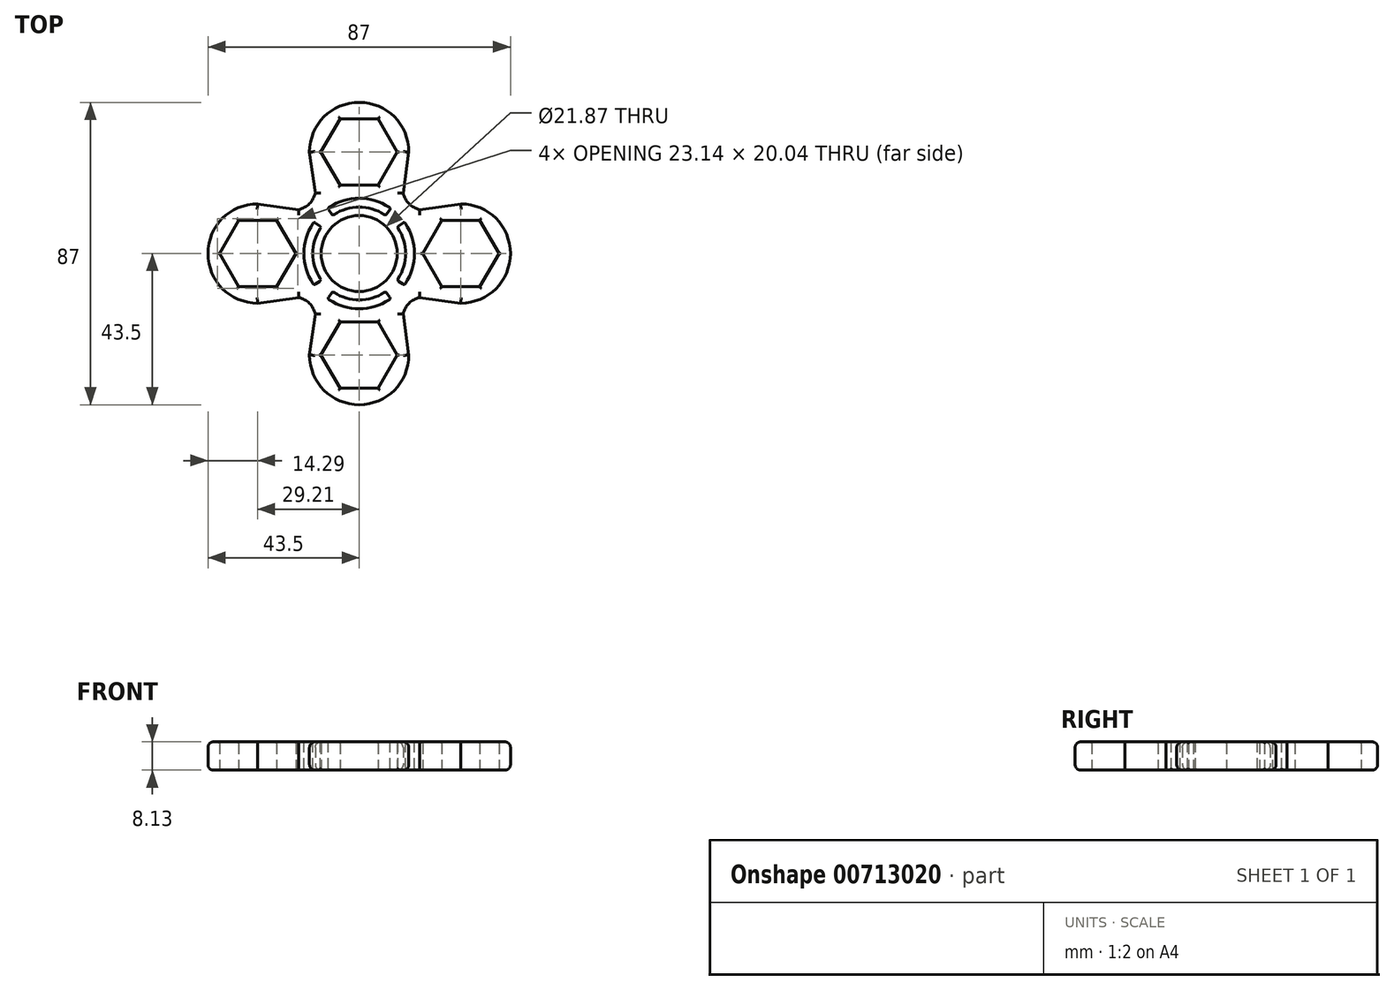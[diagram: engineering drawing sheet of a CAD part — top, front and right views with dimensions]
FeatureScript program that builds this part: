
annotation { "Feature Type Name" : "Feature", "Feature Type Description" : "" }
export const myFeature = defineFeature(function(context is Context, id is Id, definition is map)
    precondition{}
    {
        {
            var Q0;
            Q0=qCreatedBy(makeId("Top.planeOp"),FACE);
            var sketch = newSketch(context, id + "F0", { "sketchPlane" : qUnion([Q0])});
            skCircle(sketch, "E0", {"center": v(0, 0) * mm, "radius": 10.93 * mm});
            skLineSegment(sketch, "E1", {"start": v(0, 32.8) * mm, "end": v(0, -37.97) * mm, "construction": true});
            skLineSegment(sketch, "E2", {"start": v(-47.87, 0) * mm, "end": v(62.97, 0) * mm, "construction": true});
            skCircle(sketch, "E3", {"center": v(29.21, 0) * mm, "radius": 7.94 * mm});
            skCircle(sketch, "E4", {"center": v(0, 29.21) * mm, "radius": 7.94 * mm});
            skCircle(sketch, "E5", {"center": v(-29.21, 0) * mm, "radius": 7.94 * mm});
            skCircle(sketch, "E6", {"center": v(0, -29.21) * mm, "radius": 7.94 * mm});
            skArc(sketch, "E7", {"start": v(14.29, 29.21) * mm, "mid": v(0, 43.5) * mm, "end": v(-14.29, 29.21) * mm});
            skArc(sketch, "E8", {"start": v(29.21, -14.29) * mm, "mid": v(43.5, 0) * mm, "end": v(29.21, 14.29) * mm});
            skArc(sketch, "E9", {"start": v(-14.29, -29.21) * mm, "mid": v(0, -43.5) * mm, "end": v(14.29, -29.21) * mm});
            skArc(sketch, "E10", {"start": v(-29.21, 14.29) * mm, "mid": v(-43.5, 0) * mm, "end": v(-29.21, -14.29) * mm});
            skPoint(sketch, "E11.visualSharp", {"position": v(-11.05, 11.05) * mm});
            skArc(sketch, "E11.filletArc", {"start": v(-17.4, 12.64) * mm, "mid": v(-14.33, 14.33) * mm, "end": v(-12.64, 17.4) * mm});
            skPoint(sketch, "E12.visualSharp", {"position": v(11.05, 11.05) * mm});
            skArc(sketch, "E12.filletArc", {"start": v(12.64, 17.4) * mm, "mid": v(14.33, 14.33) * mm, "end": v(17.4, 12.64) * mm});
            skArc(sketch, "E13.MirrorCS", {"start": v(-17.4, -12.64) * mm, "mid": v(-14.33, -14.33) * mm, "end": v(-12.64, -17.4) * mm});
            skArc(sketch, "E14.MirrorCS", {"start": v(12.64, -17.4) * mm, "mid": v(14.33, -14.33) * mm, "end": v(17.4, -12.64) * mm});
            skLineSegment(sketch, "E15", {"start": v(-14.29, -29.21) * mm, "end": v(-12.64, -17.4) * mm});
            skLineSegment(sketch, "E16", {"start": v(14.29, -29.2) * mm, "end": v(12.64, -17.4) * mm});
            skLineSegment(sketch, "E17", {"start": v(17.4, -12.64) * mm, "end": v(29.21, -14.29) * mm});
            skLineSegment(sketch, "E18", {"start": v(17.4, 12.64) * mm, "end": v(29.21, 14.29) * mm});
            skLineSegment(sketch, "E19", {"start": v(12.64, 17.4) * mm, "end": v(14.29, 29.21) * mm});
            skLineSegment(sketch, "E20", {"start": v(-14.29, 29.21) * mm, "end": v(-12.64, 17.4) * mm});
            skLineSegment(sketch, "E21", {"start": v(-17.4, 12.64) * mm, "end": v(-29.2, 14.29) * mm});
            skLineSegment(sketch, "E22", {"start": v(-29.2, -14.29) * mm, "end": v(-17.4, -12.64) * mm});
            skCircle(sketch, "E23.cCircle", {"center": v(0, 29.21) * mm, "radius": 9.51 * mm, "construction": true});
            skLineSegment(sketch, "E23.0", {"start": v(10.99, 29.21) * mm, "end": v(5.5, 19.7) * mm});
            skLineSegment(sketch, "E23.1", {"start": v(5.5, 19.7) * mm, "end": v(-5.5, 19.7) * mm});
            skLineSegment(sketch, "E23.2", {"start": v(-5.5, 19.7) * mm, "end": v(-10.99, 29.21) * mm});
            skLineSegment(sketch, "E23.3", {"start": v(-10.99, 29.21) * mm, "end": v(-5.5, 38.72) * mm});
            skLineSegment(sketch, "E23.4", {"start": v(-5.5, 38.72) * mm, "end": v(5.5, 38.72) * mm});
            skLineSegment(sketch, "E23.5", {"start": v(5.5, 38.72) * mm, "end": v(10.99, 29.21) * mm});
            skPoint(sketch, "E23.0.midPoint", {"position": v(8.24, 24.45) * mm});
            skCircle(sketch, "E24.cCircle", {"center": v(29.21, 0) * mm, "radius": 9.51 * mm, "construction": true});
            skLineSegment(sketch, "E24.0", {"start": v(40.2, 0) * mm, "end": v(34.7, -9.51) * mm});
            skLineSegment(sketch, "E24.1", {"start": v(34.7, -9.51) * mm, "end": v(23.72, -9.51) * mm});
            skLineSegment(sketch, "E24.2", {"start": v(23.72, -9.51) * mm, "end": v(18.22, 0) * mm});
            skLineSegment(sketch, "E24.3", {"start": v(18.22, 0) * mm, "end": v(23.72, 9.51) * mm});
            skLineSegment(sketch, "E24.4", {"start": v(23.72, 9.51) * mm, "end": v(34.7, 9.51) * mm});
            skLineSegment(sketch, "E24.5", {"start": v(34.7, 9.51) * mm, "end": v(40.2, 0) * mm});
            skPoint(sketch, "E24.0.midPoint", {"position": v(37.45, -4.76) * mm});
            skCircle(sketch, "E25.cCircle", {"center": v(0, -29.21) * mm, "radius": 9.51 * mm, "construction": true});
            skLineSegment(sketch, "E25.0", {"start": v(10.99, -29.2) * mm, "end": v(5.5, -38.72) * mm});
            skLineSegment(sketch, "E25.1", {"start": v(5.5, -38.72) * mm, "end": v(-5.5, -38.72) * mm});
            skLineSegment(sketch, "E25.2", {"start": v(-5.5, -38.72) * mm, "end": v(-10.99, -29.2) * mm});
            skLineSegment(sketch, "E25.3", {"start": v(-10.99, -29.21) * mm, "end": v(-5.5, -19.7) * mm});
            skLineSegment(sketch, "E25.4", {"start": v(-5.5, -19.7) * mm, "end": v(5.5, -19.7) * mm});
            skLineSegment(sketch, "E25.5", {"start": v(5.5, -19.7) * mm, "end": v(10.99, -29.21) * mm});
            skPoint(sketch, "E25.0.midPoint", {"position": v(8.24, -33.97) * mm});
            skPoint(sketch, "E26.0.midPoint", {"position": v(-0.58, -16.53) * mm});
            skCircle(sketch, "E27.cCircle", {"center": v(-29.21, 0) * mm, "radius": 9.51 * mm, "construction": true});
            skLineSegment(sketch, "E27.0", {"start": v(-18.22, 0) * mm, "end": v(-23.72, -9.51) * mm});
            skLineSegment(sketch, "E27.1", {"start": v(-23.72, -9.51) * mm, "end": v(-34.7, -9.51) * mm});
            skLineSegment(sketch, "E27.2", {"start": v(-34.7, -9.51) * mm, "end": v(-40.2, 0) * mm});
            skLineSegment(sketch, "E27.3", {"start": v(-40.2, 0) * mm, "end": v(-34.7, 9.51) * mm});
            skLineSegment(sketch, "E27.4", {"start": v(-34.7, 9.51) * mm, "end": v(-23.72, 9.51) * mm});
            skLineSegment(sketch, "E27.5", {"start": v(-23.72, 9.51) * mm, "end": v(-18.22, 0) * mm});
            skPoint(sketch, "E27.0.midPoint", {"position": v(-20.97, -4.76) * mm});
            skSolve(sketch);
        }
        {
            var Q0;
            Q0=qSketchRegion(id+"F0",true);
            extrude(context, id + "F1", {"entities" : qUnion([Q0]), "depth" : 8.13 * mm, "offsetDistance" : 25.4 * mm});
        }
        {
            var Q0;
            Q0=makeQuery(id+"F1.opExtrude","CAP_EDGE",EDGE,{"disambiguationData":[OSD([sQuery(id+"F0.wireOp",EDGE,"E10")])],"isStart":true});
            var Q1;
            Q1=makeQuery(id+"F1.opExtrude","CAP_EDGE",EDGE,{"disambiguationData":[OSD([sQuery(id+"F0.wireOp",EDGE,"E22")])],"isStart":true});
            var Q2;
            Q2=makeQuery(id+"F1.opExtrude","CAP_EDGE",EDGE,{"disambiguationData":[OSD([sQuery(id+"F0.wireOp",EDGE,"E13.MirrorCS")])],"isStart":true});
            var Q3;
            Q3=makeQuery(id+"F1.opExtrude","CAP_EDGE",EDGE,{"disambiguationData":[OSD([sQuery(id+"F0.wireOp",EDGE,"E15")])],"isStart":true});
            var Q4;
            Q4=makeQuery(id+"F1.opExtrude","CAP_EDGE",EDGE,{"disambiguationData":[OSD([sQuery(id+"F0.wireOp",EDGE,"E9")])],"isStart":true});
            var Q5;
            Q5=makeQuery(id+"F1.opExtrude","CAP_EDGE",EDGE,{"disambiguationData":[OSD([sQuery(id+"F0.wireOp",EDGE,"E16")])],"isStart":true});
            var Q6;
            Q6=makeQuery(id+"F1.opExtrude","CAP_EDGE",EDGE,{"disambiguationData":[OSD([sQuery(id+"F0.wireOp",EDGE,"E14.MirrorCS")])],"isStart":true});
            var Q7;
            Q7=makeQuery(id+"F1.opExtrude","CAP_EDGE",EDGE,{"disambiguationData":[OSD([sQuery(id+"F0.wireOp",EDGE,"E17")])],"isStart":true});
            var Q8;
            Q8=makeQuery(id+"F1.opExtrude","CAP_EDGE",EDGE,{"disambiguationData":[OSD([sQuery(id+"F0.wireOp",EDGE,"E8")])],"isStart":true});
            var Q9;
            Q9=makeQuery(id+"F1.opExtrude","CAP_EDGE",EDGE,{"disambiguationData":[OSD([sQuery(id+"F0.wireOp",EDGE,"E18")])],"isStart":true});
            var Q10;
            Q10=makeQuery(id+"F1.opExtrude","CAP_EDGE",EDGE,{"disambiguationData":[OSD([sQuery(id+"F0.wireOp",EDGE,"E12.filletArc")])],"isStart":true});
            var Q11;
            Q11=makeQuery(id+"F1.opExtrude","CAP_EDGE",EDGE,{"disambiguationData":[OSD([sQuery(id+"F0.wireOp",EDGE,"E19")])],"isStart":true});
            var Q12;
            Q12=makeQuery(id+"F1.opExtrude","CAP_EDGE",EDGE,{"disambiguationData":[OSD([sQuery(id+"F0.wireOp",EDGE,"E7")])],"isStart":true});
            var Q13;
            Q13=makeQuery(id+"F1.opExtrude","CAP_EDGE",EDGE,{"disambiguationData":[OSD([sQuery(id+"F0.wireOp",EDGE,"E20")])],"isStart":true});
            var Q14;
            Q14=makeQuery(id+"F1.opExtrude","CAP_EDGE",EDGE,{"disambiguationData":[OSD([sQuery(id+"F0.wireOp",EDGE,"E11.filletArc")])],"isStart":true});
            var Q15;
            Q15=makeQuery(id+"F1.opExtrude","CAP_EDGE",EDGE,{"disambiguationData":[OSD([sQuery(id+"F0.wireOp",EDGE,"E21")])],"isStart":true});
            var Q16;
            Q16=makeQuery(id+"F1.opExtrude","CAP_EDGE",EDGE,{"disambiguationData":[OSD([sQuery(id+"F0.wireOp",EDGE,"E10")])],"isStart":false});
            var Q17;
            Q17=makeQuery(id+"F1.opExtrude","CAP_EDGE",EDGE,{"disambiguationData":[OSD([sQuery(id+"F0.wireOp",EDGE,"E22")])],"isStart":false});
            var Q18;
            Q18=makeQuery(id+"F1.opExtrude","CAP_EDGE",EDGE,{"disambiguationData":[OSD([sQuery(id+"F0.wireOp",EDGE,"E13.MirrorCS")])],"isStart":false});
            var Q19;
            Q19=makeQuery(id+"F1.opExtrude","CAP_EDGE",EDGE,{"disambiguationData":[OSD([sQuery(id+"F0.wireOp",EDGE,"E21")])],"isStart":false});
            var Q20;
            Q20=makeQuery(id+"F1.opExtrude","CAP_EDGE",EDGE,{"disambiguationData":[OSD([sQuery(id+"F0.wireOp",EDGE,"E11.filletArc")])],"isStart":false});
            var Q21;
            Q21=makeQuery(id+"F1.opExtrude","CAP_EDGE",EDGE,{"disambiguationData":[OSD([sQuery(id+"F0.wireOp",EDGE,"E20")])],"isStart":false});
            var Q22;
            Q22=makeQuery(id+"F1.opExtrude","CAP_EDGE",EDGE,{"disambiguationData":[OSD([sQuery(id+"F0.wireOp",EDGE,"E7")])],"isStart":false});
            var Q23;
            Q23=makeQuery(id+"F1.opExtrude","CAP_EDGE",EDGE,{"disambiguationData":[OSD([sQuery(id+"F0.wireOp",EDGE,"E19")])],"isStart":false});
            var Q24;
            Q24=makeQuery(id+"F1.opExtrude","CAP_EDGE",EDGE,{"disambiguationData":[OSD([sQuery(id+"F0.wireOp",EDGE,"E8")])],"isStart":false});
            var Q25;
            Q25=makeQuery(id+"F1.opExtrude","CAP_EDGE",EDGE,{"disambiguationData":[OSD([sQuery(id+"F0.wireOp",EDGE,"E17")])],"isStart":false});
            var Q26;
            Q26=makeQuery(id+"F1.opExtrude","CAP_EDGE",EDGE,{"disambiguationData":[OSD([sQuery(id+"F0.wireOp",EDGE,"E14.MirrorCS")])],"isStart":false});
            var Q27;
            Q27=makeQuery(id+"F1.opExtrude","CAP_EDGE",EDGE,{"disambiguationData":[OSD([sQuery(id+"F0.wireOp",EDGE,"E16")])],"isStart":false});
            var Q28;
            Q28=makeQuery(id+"F1.opExtrude","CAP_EDGE",EDGE,{"disambiguationData":[OSD([sQuery(id+"F0.wireOp",EDGE,"E9")])],"isStart":false});
            var Q29;
            Q29=makeQuery(id+"F1.opExtrude","CAP_EDGE",EDGE,{"disambiguationData":[OSD([sQuery(id+"F0.wireOp",EDGE,"E15")])],"isStart":false});
            var Q30;
            Q30=makeQuery(id+"F1.opExtrude","CAP_EDGE",EDGE,{"disambiguationData":[OSD([sQuery(id+"F0.wireOp",EDGE,"E12.filletArc")])],"isStart":false});
            var Q31;
            Q31=makeQuery(id+"F1.opExtrude","CAP_EDGE",EDGE,{"disambiguationData":[OSD([sQuery(id+"F0.wireOp",EDGE,"E18")])],"isStart":false});
            fillet(context, id + "F2", {"entities" : qUnion([Q0, Q1, Q2, Q3, Q4, Q5, Q6, Q7, Q8, Q9, Q10, Q11, Q12, Q13, Q14, Q15, Q16, Q17, Q18, Q19, Q20, Q21, Q22, Q23, Q24, Q25, Q26, Q27, Q28, Q29, Q30, Q31]), "radius" : 1.57 * mm, "allowEdgeOverflow" : false});
        }
        {
            var Q0;
            Q0=makeQuery(id+"F1.opExtrude","CAP_EDGE",EDGE,{"disambiguationData":[OSD([sQuery(id+"F0.wireOp",EDGE,"E5")])],"isStart":false});
            var Q1;
            Q1=makeQuery(id+"F1.opExtrude","CAP_EDGE",EDGE,{"disambiguationData":[OSD([sQuery(id+"F0.wireOp",EDGE,"E4")])],"isStart":false});
            var Q2;
            Q2=makeQuery(id+"F1.opExtrude","CAP_EDGE",EDGE,{"disambiguationData":[OSD([sQuery(id+"F0.wireOp",EDGE,"E0")])],"isStart":false});
            var Q3;
            Q3=makeQuery(id+"F1.opExtrude","CAP_EDGE",EDGE,{"disambiguationData":[OSD([sQuery(id+"F0.wireOp",EDGE,"E3")])],"isStart":false});
            var Q4;
            Q4=makeQuery(id+"F1.opExtrude","CAP_EDGE",EDGE,{"disambiguationData":[OSD([sQuery(id+"F0.wireOp",EDGE,"E6")])],"isStart":false});
            var Q5;
            Q5=makeQuery(id+"F1.opExtrude","CAP_EDGE",EDGE,{"disambiguationData":[OSD([sQuery(id+"F0.wireOp",EDGE,"E6")])],"isStart":true});
            var Q6;
            Q6=makeQuery(id+"F1.opExtrude","CAP_EDGE",EDGE,{"disambiguationData":[OSD([sQuery(id+"F0.wireOp",EDGE,"E5")])],"isStart":true});
            var Q7;
            Q7=makeQuery(id+"F1.opExtrude","CAP_EDGE",EDGE,{"disambiguationData":[OSD([sQuery(id+"F0.wireOp",EDGE,"E0")])],"isStart":true});
            var Q8;
            Q8=makeQuery(id+"F1.opExtrude","CAP_EDGE",EDGE,{"disambiguationData":[OSD([sQuery(id+"F0.wireOp",EDGE,"E3")])],"isStart":true});
            var Q9;
            Q9=makeQuery(id+"F1.opExtrude","CAP_EDGE",EDGE,{"disambiguationData":[OSD([sQuery(id+"F0.wireOp",EDGE,"E4")])],"isStart":true});
            fillet(context, id + "F3", {"entities" : qUnion([Q0, Q1, Q2, Q3, Q4, Q5, Q6, Q7, Q8, Q9]), "radius" : 0.5 * mm, "tangentPropagation" : true, "allowEdgeOverflow" : false});
        }
        {
            var Q0;
            Q0=makeQuery(id+"F1.opExtrude","CAP_EDGE",EDGE,{"disambiguationData":[OSD([sQuery(id+"F0.wireOp",EDGE,"E25.4")])],"isStart":false});
            var Q1;
            Q1=makeQuery(id+"F1.opExtrude","CAP_EDGE",EDGE,{"disambiguationData":[OSD([sQuery(id+"F0.wireOp",EDGE,"E24.4")])],"isStart":false});
            var Q2;
            Q2=makeQuery(id+"F1.opExtrude","CAP_EDGE",EDGE,{"disambiguationData":[OSD([sQuery(id+"F0.wireOp",EDGE,"E23.5")])],"isStart":false});
            var Q3;
            Q3=makeQuery(id+"F1.opExtrude","CAP_EDGE",EDGE,{"disambiguationData":[OSD([sQuery(id+"F0.wireOp",EDGE,"E27.5")])],"isStart":false});
            var Q4;
            Q4=makeQuery(id+"F1.opExtrude","CAP_EDGE",EDGE,{"disambiguationData":[OSD([sQuery(id+"F0.wireOp",EDGE,"E27.4")])],"isStart":false});
            var Q5;
            Q5=makeQuery(id+"F1.opExtrude","CAP_EDGE",EDGE,{"disambiguationData":[OSD([sQuery(id+"F0.wireOp",EDGE,"E27.3")])],"isStart":false});
            var Q6;
            Q6=makeQuery(id+"F1.opExtrude","CAP_EDGE",EDGE,{"disambiguationData":[OSD([sQuery(id+"F0.wireOp",EDGE,"E27.2")])],"isStart":false});
            var Q7;
            Q7=makeQuery(id+"F1.opExtrude","CAP_EDGE",EDGE,{"disambiguationData":[OSD([sQuery(id+"F0.wireOp",EDGE,"E27.1")])],"isStart":false});
            var Q8;
            Q8=makeQuery(id+"F1.opExtrude","CAP_EDGE",EDGE,{"disambiguationData":[OSD([sQuery(id+"F0.wireOp",EDGE,"E27.0")])],"isStart":false});
            var Q9;
            Q9=makeQuery(id+"F1.opExtrude","CAP_EDGE",EDGE,{"disambiguationData":[OSD([sQuery(id+"F0.wireOp",EDGE,"E25.3")])],"isStart":false});
            var Q10;
            Q10=makeQuery(id+"F1.opExtrude","CAP_EDGE",EDGE,{"disambiguationData":[OSD([sQuery(id+"F0.wireOp",EDGE,"E25.5")])],"isStart":false});
            var Q11;
            Q11=makeQuery(id+"F1.opExtrude","CAP_EDGE",EDGE,{"disambiguationData":[OSD([sQuery(id+"F0.wireOp",EDGE,"E25.0")])],"isStart":false});
            var Q12;
            Q12=makeQuery(id+"F1.opExtrude","CAP_EDGE",EDGE,{"disambiguationData":[OSD([sQuery(id+"F0.wireOp",EDGE,"E25.1")])],"isStart":false});
            var Q13;
            Q13=makeQuery(id+"F1.opExtrude","CAP_EDGE",EDGE,{"disambiguationData":[OSD([sQuery(id+"F0.wireOp",EDGE,"E25.2")])],"isStart":false});
            var Q14;
            Q14=makeQuery(id+"F1.opExtrude","CAP_EDGE",EDGE,{"disambiguationData":[OSD([sQuery(id+"F0.wireOp",EDGE,"E24.3")])],"isStart":false});
            var Q15;
            Q15=makeQuery(id+"F1.opExtrude","CAP_EDGE",EDGE,{"disambiguationData":[OSD([sQuery(id+"F0.wireOp",EDGE,"E24.2")])],"isStart":false});
            var Q16;
            Q16=makeQuery(id+"F1.opExtrude","CAP_EDGE",EDGE,{"disambiguationData":[OSD([sQuery(id+"F0.wireOp",EDGE,"E24.1")])],"isStart":false});
            var Q17;
            Q17=makeQuery(id+"F1.opExtrude","CAP_EDGE",EDGE,{"disambiguationData":[OSD([sQuery(id+"F0.wireOp",EDGE,"E24.0")])],"isStart":false});
            var Q18;
            Q18=makeQuery(id+"F1.opExtrude","CAP_EDGE",EDGE,{"disambiguationData":[OSD([sQuery(id+"F0.wireOp",EDGE,"E24.5")])],"isStart":false});
            var Q19;
            Q19=makeQuery(id+"F1.opExtrude","CAP_EDGE",EDGE,{"disambiguationData":[OSD([sQuery(id+"F0.wireOp",EDGE,"E23.0")])],"isStart":false});
            var Q20;
            Q20=makeQuery(id+"F1.opExtrude","CAP_EDGE",EDGE,{"disambiguationData":[OSD([sQuery(id+"F0.wireOp",EDGE,"E23.1")])],"isStart":false});
            var Q21;
            Q21=makeQuery(id+"F1.opExtrude","CAP_EDGE",EDGE,{"disambiguationData":[OSD([sQuery(id+"F0.wireOp",EDGE,"E23.2")])],"isStart":false});
            var Q22;
            Q22=makeQuery(id+"F1.opExtrude","CAP_EDGE",EDGE,{"disambiguationData":[OSD([sQuery(id+"F0.wireOp",EDGE,"E23.3")])],"isStart":false});
            var Q23;
            Q23=makeQuery(id+"F1.opExtrude","CAP_EDGE",EDGE,{"disambiguationData":[OSD([sQuery(id+"F0.wireOp",EDGE,"E23.4")])],"isStart":false});
            var Q24;
            Q24=makeQuery(id+"F1.opExtrude","CAP_EDGE",EDGE,{"disambiguationData":[OSD([sQuery(id+"F0.wireOp",EDGE,"E27.2")])],"isStart":true});
            var Q25;
            Q25=makeQuery(id+"F1.opExtrude","CAP_EDGE",EDGE,{"disambiguationData":[OSD([sQuery(id+"F0.wireOp",EDGE,"E27.1")])],"isStart":true});
            var Q26;
            Q26=makeQuery(id+"F1.opExtrude","CAP_EDGE",EDGE,{"disambiguationData":[OSD([sQuery(id+"F0.wireOp",EDGE,"E27.0")])],"isStart":true});
            var Q27;
            Q27=makeQuery(id+"F1.opExtrude","CAP_EDGE",EDGE,{"disambiguationData":[OSD([sQuery(id+"F0.wireOp",EDGE,"E27.5")])],"isStart":true});
            var Q28;
            Q28=makeQuery(id+"F1.opExtrude","CAP_EDGE",EDGE,{"disambiguationData":[OSD([sQuery(id+"F0.wireOp",EDGE,"E27.4")])],"isStart":true});
            var Q29;
            Q29=makeQuery(id+"F1.opExtrude","CAP_EDGE",EDGE,{"disambiguationData":[OSD([sQuery(id+"F0.wireOp",EDGE,"E27.3")])],"isStart":true});
            var Q30;
            Q30=makeQuery(id+"F1.opExtrude","CAP_EDGE",EDGE,{"disambiguationData":[OSD([sQuery(id+"F0.wireOp",EDGE,"E23.2")])],"isStart":true});
            var Q31;
            Q31=makeQuery(id+"F1.opExtrude","CAP_EDGE",EDGE,{"disambiguationData":[OSD([sQuery(id+"F0.wireOp",EDGE,"E23.1")])],"isStart":true});
            var Q32;
            Q32=makeQuery(id+"F1.opExtrude","CAP_EDGE",EDGE,{"disambiguationData":[OSD([sQuery(id+"F0.wireOp",EDGE,"E23.0")])],"isStart":true});
            var Q33;
            Q33=makeQuery(id+"F1.opExtrude","CAP_EDGE",EDGE,{"disambiguationData":[OSD([sQuery(id+"F0.wireOp",EDGE,"E23.5")])],"isStart":true});
            var Q34;
            Q34=makeQuery(id+"F1.opExtrude","CAP_EDGE",EDGE,{"disambiguationData":[OSD([sQuery(id+"F0.wireOp",EDGE,"E23.4")])],"isStart":true});
            var Q35;
            Q35=makeQuery(id+"F1.opExtrude","CAP_EDGE",EDGE,{"disambiguationData":[OSD([sQuery(id+"F0.wireOp",EDGE,"E23.3")])],"isStart":true});
            var Q36;
            Q36=makeQuery(id+"F1.opExtrude","CAP_EDGE",EDGE,{"disambiguationData":[OSD([sQuery(id+"F0.wireOp",EDGE,"E24.2")])],"isStart":true});
            var Q37;
            Q37=makeQuery(id+"F1.opExtrude","CAP_EDGE",EDGE,{"disambiguationData":[OSD([sQuery(id+"F0.wireOp",EDGE,"E24.1")])],"isStart":true});
            var Q38;
            Q38=makeQuery(id+"F1.opExtrude","CAP_EDGE",EDGE,{"disambiguationData":[OSD([sQuery(id+"F0.wireOp",EDGE,"E24.0")])],"isStart":true});
            var Q39;
            Q39=makeQuery(id+"F1.opExtrude","CAP_EDGE",EDGE,{"disambiguationData":[OSD([sQuery(id+"F0.wireOp",EDGE,"E24.5")])],"isStart":true});
            var Q40;
            Q40=makeQuery(id+"F1.opExtrude","CAP_EDGE",EDGE,{"disambiguationData":[OSD([sQuery(id+"F0.wireOp",EDGE,"E24.4")])],"isStart":true});
            var Q41;
            Q41=makeQuery(id+"F1.opExtrude","CAP_EDGE",EDGE,{"disambiguationData":[OSD([sQuery(id+"F0.wireOp",EDGE,"E24.3")])],"isStart":true});
            var Q42;
            Q42=makeQuery(id+"F1.opExtrude","CAP_EDGE",EDGE,{"disambiguationData":[OSD([sQuery(id+"F0.wireOp",EDGE,"E25.4")])],"isStart":true});
            var Q43;
            Q43=makeQuery(id+"F1.opExtrude","CAP_EDGE",EDGE,{"disambiguationData":[OSD([sQuery(id+"F0.wireOp",EDGE,"E25.3")])],"isStart":true});
            var Q44;
            Q44=makeQuery(id+"F1.opExtrude","CAP_EDGE",EDGE,{"disambiguationData":[OSD([sQuery(id+"F0.wireOp",EDGE,"E25.2")])],"isStart":true});
            var Q45;
            Q45=makeQuery(id+"F1.opExtrude","CAP_EDGE",EDGE,{"disambiguationData":[OSD([sQuery(id+"F0.wireOp",EDGE,"E25.1")])],"isStart":true});
            var Q46;
            Q46=makeQuery(id+"F1.opExtrude","CAP_EDGE",EDGE,{"disambiguationData":[OSD([sQuery(id+"F0.wireOp",EDGE,"E25.0")])],"isStart":true});
            var Q47;
            Q47=makeQuery(id+"F1.opExtrude","CAP_EDGE",EDGE,{"disambiguationData":[OSD([sQuery(id+"F0.wireOp",EDGE,"E25.5")])],"isStart":true});
            fillet(context, id + "F4", {"entities" : qUnion([Q0, Q1, Q2, Q3, Q4, Q5, Q6, Q7, Q8, Q9, Q10, Q11, Q12, Q13, Q14, Q15, Q16, Q17, Q18, Q19, Q20, Q21, Q22, Q23, Q24, Q25, Q26, Q27, Q28, Q29, Q30, Q31, Q32, Q33, Q34, Q35, Q36, Q37, Q38, Q39, Q40, Q41, Q42, Q43, Q44, Q45, Q46, Q47]), "radius" : 0.5 * mm, "tangentPropagation" : true, "allowEdgeOverflow" : false});
        }
        {
            var Q0;
            Q0=makeQuery(id+"F1.opExtrude","CAP_FACE",FACE,{"disambiguationData":[OSD([sQuery(id+"F0.wireOp",EDGE,"E0"),sQuery(id+"F0.wireOp",EDGE,"E7"),sQuery(id+"F0.wireOp",EDGE,"E8"),sQuery(id+"F0.wireOp",EDGE,"E9"),sQuery(id+"F0.wireOp",EDGE,"E10"),sQuery(id+"F0.wireOp",EDGE,"E11.filletArc"),sQuery(id+"F0.wireOp",EDGE,"E12.filletArc"),sQuery(id+"F0.wireOp",EDGE,"E13.MirrorCS"),sQuery(id+"F0.wireOp",EDGE,"E14.MirrorCS"),sQuery(id+"F0.wireOp",EDGE,"E15"),sQuery(id+"F0.wireOp",EDGE,"E16"),sQuery(id+"F0.wireOp",EDGE,"E17"),sQuery(id+"F0.wireOp",EDGE,"E18"),sQuery(id+"F0.wireOp",EDGE,"E19"),sQuery(id+"F0.wireOp",EDGE,"E20"),sQuery(id+"F0.wireOp",EDGE,"E21"),sQuery(id+"F0.wireOp",EDGE,"E22"),sQuery(id+"F0.wireOp",EDGE,"E23.0"),sQuery(id+"F0.wireOp",EDGE,"E23.1"),sQuery(id+"F0.wireOp",EDGE,"E23.2"),sQuery(id+"F0.wireOp",EDGE,"E23.3"),sQuery(id+"F0.wireOp",EDGE,"E23.4"),sQuery(id+"F0.wireOp",EDGE,"E23.5"),sQuery(id+"F0.wireOp",EDGE,"E24.0"),sQuery(id+"F0.wireOp",EDGE,"E24.1"),sQuery(id+"F0.wireOp",EDGE,"E24.2"),sQuery(id+"F0.wireOp",EDGE,"E24.3"),sQuery(id+"F0.wireOp",EDGE,"E24.4"),sQuery(id+"F0.wireOp",EDGE,"E24.5"),sQuery(id+"F0.wireOp",EDGE,"E25.0"),sQuery(id+"F0.wireOp",EDGE,"E25.1"),sQuery(id+"F0.wireOp",EDGE,"E25.2"),sQuery(id+"F0.wireOp",EDGE,"E25.3"),sQuery(id+"F0.wireOp",EDGE,"E25.4"),sQuery(id+"F0.wireOp",EDGE,"E25.5"),sQuery(id+"F0.wireOp",EDGE,"E27.0"),sQuery(id+"F0.wireOp",EDGE,"E27.1"),sQuery(id+"F0.wireOp",EDGE,"E27.2"),sQuery(id+"F0.wireOp",EDGE,"E27.3"),sQuery(id+"F0.wireOp",EDGE,"E27.4"),sQuery(id+"F0.wireOp",EDGE,"E27.5")])],"isStart":false});
            var sketch = newSketch(context, id + "F5", { "sketchPlane" : qUnion([Q0])});
            skLineSegment(sketch, "E28", {"start": v(0, 19.96) * mm, "end": v(0, -20.08) * mm, "construction": true});
            skLineSegment(sketch, "E29", {"start": v(-9.1, 13) * mm, "end": v(-7.65, 10.92) * mm});
            skLineSegment(sketch, "E30", {"start": v(9.1, 13) * mm, "end": v(7.65, 10.92) * mm});
            skArc(sketch, "E31", {"start": v(9.1, 13) * mm, "mid": v(0, 15.88) * mm, "end": v(-9.1, 13) * mm});
            skArc(sketch, "E32", {"start": v(7.65, 10.92) * mm, "mid": v(0, 13.34) * mm, "end": v(-7.65, 10.92) * mm});
            skArc(sketch, "E33.1.0", {"start": v(-13, 9.1) * mm, "mid": v(-15.88, 0) * mm, "end": v(-13, -9.1) * mm});
            skLineSegment(sketch, "E33.1.1", {"start": v(-13, -9.1) * mm, "end": v(-10.92, -7.65) * mm});
            skArc(sketch, "E33.1.2", {"start": v(-10.92, 7.65) * mm, "mid": v(-13.34, 0) * mm, "end": v(-10.92, -7.65) * mm});
            skLineSegment(sketch, "E33.1.3", {"start": v(-13, 9.1) * mm, "end": v(-10.92, 7.65) * mm});
            skArc(sketch, "E33.2.0", {"start": v(-9.1, -13) * mm, "mid": v(0, -15.87) * mm, "end": v(9.1, -13) * mm});
            skLineSegment(sketch, "E33.2.1", {"start": v(9.1, -13) * mm, "end": v(7.65, -10.92) * mm});
            skArc(sketch, "E33.2.2", {"start": v(-7.65, -10.92) * mm, "mid": v(0, -13.33) * mm, "end": v(7.65, -10.92) * mm});
            skLineSegment(sketch, "E33.2.3", {"start": v(-9.1, -13) * mm, "end": v(-7.65, -10.92) * mm});
            skLineSegment(sketch, "E34.4.3.0", {"start": v(13, 9.1) * mm, "end": v(10.92, 7.65) * mm});
            skArc(sketch, "E34.6.3.0", {"start": v(13, -9.1) * mm, "mid": v(15.87, 0) * mm, "end": v(13, 9.1) * mm});
            skArc(sketch, "E34.7.3.0", {"start": v(10.92, -7.65) * mm, "mid": v(13.34, 0) * mm, "end": v(10.92, 7.65) * mm});
            skLineSegment(sketch, "E34.11.3.0", {"start": v(13, -9.1) * mm, "end": v(10.92, -7.65) * mm});
            skSolve(sketch);
        }
        {
            var Q0;
            Q0 = qSketchRegion(id + "F5", true);
            extrude(context, id + "F6", {"entities" : qUnion([Q0]), "operationType" : NewBodyOperationType.REMOVE, "oppositeDirection" : true, "depth" : 25.4 * mm, "offsetDistance" : 25.4 * mm});
        }
        {
            var Q0;
            Q0=makeQuery(id+"F6.boolean.opBoolean","COPY",EDGE,{"derivedFrom":makeQuery(id+"F6.opExtrude","SWEPT_EDGE",EDGE,{"disambiguationData":[OSD([sQuery(id+"F5.wireOp",EDGE,"E30"),sQuery(id+"F5.wireOp",EDGE,"E31")])]})});
            var Q1;
            Q1=makeQuery(id+"F6.boolean.opBoolean","COPY",EDGE,{"derivedFrom":makeQuery(id+"F6.opExtrude","SWEPT_EDGE",EDGE,{"disambiguationData":[OSD([sQuery(id+"F5.wireOp",EDGE,"E30"),sQuery(id+"F5.wireOp",EDGE,"E32")])]})});
            var Q2;
            Q2=makeQuery(id+"F6.boolean.opBoolean","COPY",EDGE,{"derivedFrom":makeQuery(id+"F6.opExtrude","CAP_EDGE",EDGE,{"disambiguationData":[OSD([sQuery(id+"F5.wireOp",EDGE,"E30")])],"isStart":true})});
            var Q3;
            Q3=makeQuery(id+"F6.boolean.opBoolean","COPY",EDGE,{"derivedFrom":makeQuery(id+"F6.opExtrude","SWEPT_EDGE",EDGE,{"disambiguationData":[OSD([sQuery(id+"F5.wireOp",EDGE,"E29"),sQuery(id+"F5.wireOp",EDGE,"E31")])]})});
            var Q4;
            Q4=makeQuery(id+"F6.boolean.opBoolean","COPY",EDGE,{"derivedFrom":makeQuery(id+"F6.opExtrude","SWEPT_EDGE",EDGE,{"disambiguationData":[OSD([sQuery(id+"F5.wireOp",EDGE,"E29"),sQuery(id+"F5.wireOp",EDGE,"E32")])]})});
            var Q5;
            Q5=makeQuery(id+"F6.boolean.opBoolean","INTERSECT",EDGE,{"derivedFrom":[makeQuery(id+"F1.opExtrude","CAP_FACE",FACE,{"disambiguationData":[OSD([sQuery(id+"F0.wireOp",EDGE,"E0"),sQuery(id+"F0.wireOp",EDGE,"E7"),sQuery(id+"F0.wireOp",EDGE,"E8"),sQuery(id+"F0.wireOp",EDGE,"E9"),sQuery(id+"F0.wireOp",EDGE,"E10"),sQuery(id+"F0.wireOp",EDGE,"E11.filletArc"),sQuery(id+"F0.wireOp",EDGE,"E12.filletArc"),sQuery(id+"F0.wireOp",EDGE,"E13.MirrorCS"),sQuery(id+"F0.wireOp",EDGE,"E14.MirrorCS"),sQuery(id+"F0.wireOp",EDGE,"E15"),sQuery(id+"F0.wireOp",EDGE,"E16"),sQuery(id+"F0.wireOp",EDGE,"E17"),sQuery(id+"F0.wireOp",EDGE,"E18"),sQuery(id+"F0.wireOp",EDGE,"E19"),sQuery(id+"F0.wireOp",EDGE,"E20"),sQuery(id+"F0.wireOp",EDGE,"E21"),sQuery(id+"F0.wireOp",EDGE,"E22"),sQuery(id+"F0.wireOp",EDGE,"E23.0"),sQuery(id+"F0.wireOp",EDGE,"E23.1"),sQuery(id+"F0.wireOp",EDGE,"E23.2"),sQuery(id+"F0.wireOp",EDGE,"E23.3"),sQuery(id+"F0.wireOp",EDGE,"E23.4"),sQuery(id+"F0.wireOp",EDGE,"E23.5"),sQuery(id+"F0.wireOp",EDGE,"E24.0"),sQuery(id+"F0.wireOp",EDGE,"E24.1"),sQuery(id+"F0.wireOp",EDGE,"E24.2"),sQuery(id+"F0.wireOp",EDGE,"E24.3"),sQuery(id+"F0.wireOp",EDGE,"E24.4"),sQuery(id+"F0.wireOp",EDGE,"E24.5"),sQuery(id+"F0.wireOp",EDGE,"E25.0"),sQuery(id+"F0.wireOp",EDGE,"E25.1"),sQuery(id+"F0.wireOp",EDGE,"E25.2"),sQuery(id+"F0.wireOp",EDGE,"E25.3"),sQuery(id+"F0.wireOp",EDGE,"E25.4"),sQuery(id+"F0.wireOp",EDGE,"E25.5"),sQuery(id+"F0.wireOp",EDGE,"E27.0"),sQuery(id+"F0.wireOp",EDGE,"E27.1"),sQuery(id+"F0.wireOp",EDGE,"E27.2"),sQuery(id+"F0.wireOp",EDGE,"E27.3"),sQuery(id+"F0.wireOp",EDGE,"E27.4"),sQuery(id+"F0.wireOp",EDGE,"E27.5")])],"isStart":true}),makeQuery(id+"F6.opExtrude","SWEPT_FACE",FACE,{"disambiguationData":[OSD([sQuery(id+"F5.wireOp",EDGE,"E31")])]})]});
            var Q6;
            Q6=makeQuery(id+"F6.boolean.opBoolean","COPY",EDGE,{"derivedFrom":makeQuery(id+"F6.opExtrude","CAP_EDGE",EDGE,{"disambiguationData":[OSD([sQuery(id+"F5.wireOp",EDGE,"E33.1.3")])],"isStart":true})});
            var Q7;
            Q7=makeQuery(id+"F6.boolean.opBoolean","COPY",EDGE,{"derivedFrom":makeQuery(id+"F6.opExtrude","CAP_EDGE",EDGE,{"disambiguationData":[OSD([sQuery(id+"F5.wireOp",EDGE,"E34.6.3.0")])],"isStart":true})});
            var Q8;
            Q8=makeQuery(id+"F6.boolean.opBoolean","COPY",EDGE,{"derivedFrom":makeQuery(id+"F6.opExtrude","CAP_EDGE",EDGE,{"disambiguationData":[OSD([sQuery(id+"F5.wireOp",EDGE,"E33.2.0")])],"isStart":true})});
            var Q9;
            Q9=makeQuery(id+"F6.boolean.opBoolean","INTERSECT",EDGE,{"derivedFrom":[makeQuery(id+"F1.opExtrude","CAP_FACE",FACE,{"disambiguationData":[OSD([sQuery(id+"F0.wireOp",EDGE,"E0"),sQuery(id+"F0.wireOp",EDGE,"E7"),sQuery(id+"F0.wireOp",EDGE,"E8"),sQuery(id+"F0.wireOp",EDGE,"E9"),sQuery(id+"F0.wireOp",EDGE,"E10"),sQuery(id+"F0.wireOp",EDGE,"E11.filletArc"),sQuery(id+"F0.wireOp",EDGE,"E12.filletArc"),sQuery(id+"F0.wireOp",EDGE,"E13.MirrorCS"),sQuery(id+"F0.wireOp",EDGE,"E14.MirrorCS"),sQuery(id+"F0.wireOp",EDGE,"E15"),sQuery(id+"F0.wireOp",EDGE,"E16"),sQuery(id+"F0.wireOp",EDGE,"E17"),sQuery(id+"F0.wireOp",EDGE,"E18"),sQuery(id+"F0.wireOp",EDGE,"E19"),sQuery(id+"F0.wireOp",EDGE,"E20"),sQuery(id+"F0.wireOp",EDGE,"E21"),sQuery(id+"F0.wireOp",EDGE,"E22"),sQuery(id+"F0.wireOp",EDGE,"E23.0"),sQuery(id+"F0.wireOp",EDGE,"E23.1"),sQuery(id+"F0.wireOp",EDGE,"E23.2"),sQuery(id+"F0.wireOp",EDGE,"E23.3"),sQuery(id+"F0.wireOp",EDGE,"E23.4"),sQuery(id+"F0.wireOp",EDGE,"E23.5"),sQuery(id+"F0.wireOp",EDGE,"E24.0"),sQuery(id+"F0.wireOp",EDGE,"E24.1"),sQuery(id+"F0.wireOp",EDGE,"E24.2"),sQuery(id+"F0.wireOp",EDGE,"E24.3"),sQuery(id+"F0.wireOp",EDGE,"E24.4"),sQuery(id+"F0.wireOp",EDGE,"E24.5"),sQuery(id+"F0.wireOp",EDGE,"E25.0"),sQuery(id+"F0.wireOp",EDGE,"E25.1"),sQuery(id+"F0.wireOp",EDGE,"E25.2"),sQuery(id+"F0.wireOp",EDGE,"E25.3"),sQuery(id+"F0.wireOp",EDGE,"E25.4"),sQuery(id+"F0.wireOp",EDGE,"E25.5"),sQuery(id+"F0.wireOp",EDGE,"E27.0"),sQuery(id+"F0.wireOp",EDGE,"E27.1"),sQuery(id+"F0.wireOp",EDGE,"E27.2"),sQuery(id+"F0.wireOp",EDGE,"E27.3"),sQuery(id+"F0.wireOp",EDGE,"E27.4"),sQuery(id+"F0.wireOp",EDGE,"E27.5")])],"isStart":true}),makeQuery(id+"F6.opExtrude","SWEPT_FACE",FACE,{"disambiguationData":[OSD([sQuery(id+"F5.wireOp",EDGE,"E33.2.0")])]})]});
            var Q10;
            Q10=makeQuery(id+"F6.boolean.opBoolean","INTERSECT",EDGE,{"derivedFrom":[makeQuery(id+"F1.opExtrude","CAP_FACE",FACE,{"disambiguationData":[OSD([sQuery(id+"F0.wireOp",EDGE,"E0"),sQuery(id+"F0.wireOp",EDGE,"E7"),sQuery(id+"F0.wireOp",EDGE,"E8"),sQuery(id+"F0.wireOp",EDGE,"E9"),sQuery(id+"F0.wireOp",EDGE,"E10"),sQuery(id+"F0.wireOp",EDGE,"E11.filletArc"),sQuery(id+"F0.wireOp",EDGE,"E12.filletArc"),sQuery(id+"F0.wireOp",EDGE,"E13.MirrorCS"),sQuery(id+"F0.wireOp",EDGE,"E14.MirrorCS"),sQuery(id+"F0.wireOp",EDGE,"E15"),sQuery(id+"F0.wireOp",EDGE,"E16"),sQuery(id+"F0.wireOp",EDGE,"E17"),sQuery(id+"F0.wireOp",EDGE,"E18"),sQuery(id+"F0.wireOp",EDGE,"E19"),sQuery(id+"F0.wireOp",EDGE,"E20"),sQuery(id+"F0.wireOp",EDGE,"E21"),sQuery(id+"F0.wireOp",EDGE,"E22"),sQuery(id+"F0.wireOp",EDGE,"E23.0"),sQuery(id+"F0.wireOp",EDGE,"E23.1"),sQuery(id+"F0.wireOp",EDGE,"E23.2"),sQuery(id+"F0.wireOp",EDGE,"E23.3"),sQuery(id+"F0.wireOp",EDGE,"E23.4"),sQuery(id+"F0.wireOp",EDGE,"E23.5"),sQuery(id+"F0.wireOp",EDGE,"E24.0"),sQuery(id+"F0.wireOp",EDGE,"E24.1"),sQuery(id+"F0.wireOp",EDGE,"E24.2"),sQuery(id+"F0.wireOp",EDGE,"E24.3"),sQuery(id+"F0.wireOp",EDGE,"E24.4"),sQuery(id+"F0.wireOp",EDGE,"E24.5"),sQuery(id+"F0.wireOp",EDGE,"E25.0"),sQuery(id+"F0.wireOp",EDGE,"E25.1"),sQuery(id+"F0.wireOp",EDGE,"E25.2"),sQuery(id+"F0.wireOp",EDGE,"E25.3"),sQuery(id+"F0.wireOp",EDGE,"E25.4"),sQuery(id+"F0.wireOp",EDGE,"E25.5"),sQuery(id+"F0.wireOp",EDGE,"E27.0"),sQuery(id+"F0.wireOp",EDGE,"E27.1"),sQuery(id+"F0.wireOp",EDGE,"E27.2"),sQuery(id+"F0.wireOp",EDGE,"E27.3"),sQuery(id+"F0.wireOp",EDGE,"E27.4"),sQuery(id+"F0.wireOp",EDGE,"E27.5")])],"isStart":true}),makeQuery(id+"F6.opExtrude","SWEPT_FACE",FACE,{"disambiguationData":[OSD([sQuery(id+"F5.wireOp",EDGE,"E33.2.2")])]})]});
            var Q11;
            Q11=makeQuery(id+"F6.boolean.opBoolean","INTERSECT",EDGE,{"derivedFrom":[makeQuery(id+"F1.opExtrude","CAP_FACE",FACE,{"disambiguationData":[OSD([sQuery(id+"F0.wireOp",EDGE,"E0"),sQuery(id+"F0.wireOp",EDGE,"E7"),sQuery(id+"F0.wireOp",EDGE,"E8"),sQuery(id+"F0.wireOp",EDGE,"E9"),sQuery(id+"F0.wireOp",EDGE,"E10"),sQuery(id+"F0.wireOp",EDGE,"E11.filletArc"),sQuery(id+"F0.wireOp",EDGE,"E12.filletArc"),sQuery(id+"F0.wireOp",EDGE,"E13.MirrorCS"),sQuery(id+"F0.wireOp",EDGE,"E14.MirrorCS"),sQuery(id+"F0.wireOp",EDGE,"E15"),sQuery(id+"F0.wireOp",EDGE,"E16"),sQuery(id+"F0.wireOp",EDGE,"E17"),sQuery(id+"F0.wireOp",EDGE,"E18"),sQuery(id+"F0.wireOp",EDGE,"E19"),sQuery(id+"F0.wireOp",EDGE,"E20"),sQuery(id+"F0.wireOp",EDGE,"E21"),sQuery(id+"F0.wireOp",EDGE,"E22"),sQuery(id+"F0.wireOp",EDGE,"E23.0"),sQuery(id+"F0.wireOp",EDGE,"E23.1"),sQuery(id+"F0.wireOp",EDGE,"E23.2"),sQuery(id+"F0.wireOp",EDGE,"E23.3"),sQuery(id+"F0.wireOp",EDGE,"E23.4"),sQuery(id+"F0.wireOp",EDGE,"E23.5"),sQuery(id+"F0.wireOp",EDGE,"E24.0"),sQuery(id+"F0.wireOp",EDGE,"E24.1"),sQuery(id+"F0.wireOp",EDGE,"E24.2"),sQuery(id+"F0.wireOp",EDGE,"E24.3"),sQuery(id+"F0.wireOp",EDGE,"E24.4"),sQuery(id+"F0.wireOp",EDGE,"E24.5"),sQuery(id+"F0.wireOp",EDGE,"E25.0"),sQuery(id+"F0.wireOp",EDGE,"E25.1"),sQuery(id+"F0.wireOp",EDGE,"E25.2"),sQuery(id+"F0.wireOp",EDGE,"E25.3"),sQuery(id+"F0.wireOp",EDGE,"E25.4"),sQuery(id+"F0.wireOp",EDGE,"E25.5"),sQuery(id+"F0.wireOp",EDGE,"E27.0"),sQuery(id+"F0.wireOp",EDGE,"E27.1"),sQuery(id+"F0.wireOp",EDGE,"E27.2"),sQuery(id+"F0.wireOp",EDGE,"E27.3"),sQuery(id+"F0.wireOp",EDGE,"E27.4"),sQuery(id+"F0.wireOp",EDGE,"E27.5")])],"isStart":true}),makeQuery(id+"F6.opExtrude","SWEPT_FACE",FACE,{"disambiguationData":[OSD([sQuery(id+"F5.wireOp",EDGE,"E33.1.0")])]})]});
            var Q12;
            Q12=makeQuery(id+"F6.boolean.opBoolean","INTERSECT",EDGE,{"derivedFrom":[makeQuery(id+"F1.opExtrude","CAP_FACE",FACE,{"disambiguationData":[OSD([sQuery(id+"F0.wireOp",EDGE,"E0"),sQuery(id+"F0.wireOp",EDGE,"E7"),sQuery(id+"F0.wireOp",EDGE,"E8"),sQuery(id+"F0.wireOp",EDGE,"E9"),sQuery(id+"F0.wireOp",EDGE,"E10"),sQuery(id+"F0.wireOp",EDGE,"E11.filletArc"),sQuery(id+"F0.wireOp",EDGE,"E12.filletArc"),sQuery(id+"F0.wireOp",EDGE,"E13.MirrorCS"),sQuery(id+"F0.wireOp",EDGE,"E14.MirrorCS"),sQuery(id+"F0.wireOp",EDGE,"E15"),sQuery(id+"F0.wireOp",EDGE,"E16"),sQuery(id+"F0.wireOp",EDGE,"E17"),sQuery(id+"F0.wireOp",EDGE,"E18"),sQuery(id+"F0.wireOp",EDGE,"E19"),sQuery(id+"F0.wireOp",EDGE,"E20"),sQuery(id+"F0.wireOp",EDGE,"E21"),sQuery(id+"F0.wireOp",EDGE,"E22"),sQuery(id+"F0.wireOp",EDGE,"E23.0"),sQuery(id+"F0.wireOp",EDGE,"E23.1"),sQuery(id+"F0.wireOp",EDGE,"E23.2"),sQuery(id+"F0.wireOp",EDGE,"E23.3"),sQuery(id+"F0.wireOp",EDGE,"E23.4"),sQuery(id+"F0.wireOp",EDGE,"E23.5"),sQuery(id+"F0.wireOp",EDGE,"E24.0"),sQuery(id+"F0.wireOp",EDGE,"E24.1"),sQuery(id+"F0.wireOp",EDGE,"E24.2"),sQuery(id+"F0.wireOp",EDGE,"E24.3"),sQuery(id+"F0.wireOp",EDGE,"E24.4"),sQuery(id+"F0.wireOp",EDGE,"E24.5"),sQuery(id+"F0.wireOp",EDGE,"E25.0"),sQuery(id+"F0.wireOp",EDGE,"E25.1"),sQuery(id+"F0.wireOp",EDGE,"E25.2"),sQuery(id+"F0.wireOp",EDGE,"E25.3"),sQuery(id+"F0.wireOp",EDGE,"E25.4"),sQuery(id+"F0.wireOp",EDGE,"E25.5"),sQuery(id+"F0.wireOp",EDGE,"E27.0"),sQuery(id+"F0.wireOp",EDGE,"E27.1"),sQuery(id+"F0.wireOp",EDGE,"E27.2"),sQuery(id+"F0.wireOp",EDGE,"E27.3"),sQuery(id+"F0.wireOp",EDGE,"E27.4"),sQuery(id+"F0.wireOp",EDGE,"E27.5")])],"isStart":true}),makeQuery(id+"F6.opExtrude","SWEPT_FACE",FACE,{"disambiguationData":[OSD([sQuery(id+"F5.wireOp",EDGE,"E33.1.2")])]})]});
            var Q13;
            Q13=makeQuery(id+"F6.boolean.opBoolean","INTERSECT",EDGE,{"derivedFrom":[makeQuery(id+"F1.opExtrude","CAP_FACE",FACE,{"disambiguationData":[OSD([sQuery(id+"F0.wireOp",EDGE,"E0"),sQuery(id+"F0.wireOp",EDGE,"E7"),sQuery(id+"F0.wireOp",EDGE,"E8"),sQuery(id+"F0.wireOp",EDGE,"E9"),sQuery(id+"F0.wireOp",EDGE,"E10"),sQuery(id+"F0.wireOp",EDGE,"E11.filletArc"),sQuery(id+"F0.wireOp",EDGE,"E12.filletArc"),sQuery(id+"F0.wireOp",EDGE,"E13.MirrorCS"),sQuery(id+"F0.wireOp",EDGE,"E14.MirrorCS"),sQuery(id+"F0.wireOp",EDGE,"E15"),sQuery(id+"F0.wireOp",EDGE,"E16"),sQuery(id+"F0.wireOp",EDGE,"E17"),sQuery(id+"F0.wireOp",EDGE,"E18"),sQuery(id+"F0.wireOp",EDGE,"E19"),sQuery(id+"F0.wireOp",EDGE,"E20"),sQuery(id+"F0.wireOp",EDGE,"E21"),sQuery(id+"F0.wireOp",EDGE,"E22"),sQuery(id+"F0.wireOp",EDGE,"E23.0"),sQuery(id+"F0.wireOp",EDGE,"E23.1"),sQuery(id+"F0.wireOp",EDGE,"E23.2"),sQuery(id+"F0.wireOp",EDGE,"E23.3"),sQuery(id+"F0.wireOp",EDGE,"E23.4"),sQuery(id+"F0.wireOp",EDGE,"E23.5"),sQuery(id+"F0.wireOp",EDGE,"E24.0"),sQuery(id+"F0.wireOp",EDGE,"E24.1"),sQuery(id+"F0.wireOp",EDGE,"E24.2"),sQuery(id+"F0.wireOp",EDGE,"E24.3"),sQuery(id+"F0.wireOp",EDGE,"E24.4"),sQuery(id+"F0.wireOp",EDGE,"E24.5"),sQuery(id+"F0.wireOp",EDGE,"E25.0"),sQuery(id+"F0.wireOp",EDGE,"E25.1"),sQuery(id+"F0.wireOp",EDGE,"E25.2"),sQuery(id+"F0.wireOp",EDGE,"E25.3"),sQuery(id+"F0.wireOp",EDGE,"E25.4"),sQuery(id+"F0.wireOp",EDGE,"E25.5"),sQuery(id+"F0.wireOp",EDGE,"E27.0"),sQuery(id+"F0.wireOp",EDGE,"E27.1"),sQuery(id+"F0.wireOp",EDGE,"E27.2"),sQuery(id+"F0.wireOp",EDGE,"E27.3"),sQuery(id+"F0.wireOp",EDGE,"E27.4"),sQuery(id+"F0.wireOp",EDGE,"E27.5")])],"isStart":true}),makeQuery(id+"F6.opExtrude","SWEPT_FACE",FACE,{"disambiguationData":[OSD([sQuery(id+"F5.wireOp",EDGE,"E33.1.1")])]})]});
            var Q14;
            Q14=makeQuery(id+"F6.boolean.opBoolean","INTERSECT",EDGE,{"derivedFrom":[makeQuery(id+"F1.opExtrude","CAP_FACE",FACE,{"disambiguationData":[OSD([sQuery(id+"F0.wireOp",EDGE,"E0"),sQuery(id+"F0.wireOp",EDGE,"E7"),sQuery(id+"F0.wireOp",EDGE,"E8"),sQuery(id+"F0.wireOp",EDGE,"E9"),sQuery(id+"F0.wireOp",EDGE,"E10"),sQuery(id+"F0.wireOp",EDGE,"E11.filletArc"),sQuery(id+"F0.wireOp",EDGE,"E12.filletArc"),sQuery(id+"F0.wireOp",EDGE,"E13.MirrorCS"),sQuery(id+"F0.wireOp",EDGE,"E14.MirrorCS"),sQuery(id+"F0.wireOp",EDGE,"E15"),sQuery(id+"F0.wireOp",EDGE,"E16"),sQuery(id+"F0.wireOp",EDGE,"E17"),sQuery(id+"F0.wireOp",EDGE,"E18"),sQuery(id+"F0.wireOp",EDGE,"E19"),sQuery(id+"F0.wireOp",EDGE,"E20"),sQuery(id+"F0.wireOp",EDGE,"E21"),sQuery(id+"F0.wireOp",EDGE,"E22"),sQuery(id+"F0.wireOp",EDGE,"E23.0"),sQuery(id+"F0.wireOp",EDGE,"E23.1"),sQuery(id+"F0.wireOp",EDGE,"E23.2"),sQuery(id+"F0.wireOp",EDGE,"E23.3"),sQuery(id+"F0.wireOp",EDGE,"E23.4"),sQuery(id+"F0.wireOp",EDGE,"E23.5"),sQuery(id+"F0.wireOp",EDGE,"E24.0"),sQuery(id+"F0.wireOp",EDGE,"E24.1"),sQuery(id+"F0.wireOp",EDGE,"E24.2"),sQuery(id+"F0.wireOp",EDGE,"E24.3"),sQuery(id+"F0.wireOp",EDGE,"E24.4"),sQuery(id+"F0.wireOp",EDGE,"E24.5"),sQuery(id+"F0.wireOp",EDGE,"E25.0"),sQuery(id+"F0.wireOp",EDGE,"E25.1"),sQuery(id+"F0.wireOp",EDGE,"E25.2"),sQuery(id+"F0.wireOp",EDGE,"E25.3"),sQuery(id+"F0.wireOp",EDGE,"E25.4"),sQuery(id+"F0.wireOp",EDGE,"E25.5"),sQuery(id+"F0.wireOp",EDGE,"E27.0"),sQuery(id+"F0.wireOp",EDGE,"E27.1"),sQuery(id+"F0.wireOp",EDGE,"E27.2"),sQuery(id+"F0.wireOp",EDGE,"E27.3"),sQuery(id+"F0.wireOp",EDGE,"E27.4"),sQuery(id+"F0.wireOp",EDGE,"E27.5")])],"isStart":true}),makeQuery(id+"F6.opExtrude","SWEPT_FACE",FACE,{"disambiguationData":[OSD([sQuery(id+"F5.wireOp",EDGE,"E33.2.1")])]})]});
            var Q15;
            Q15=makeQuery(id+"F6.boolean.opBoolean","INTERSECT",EDGE,{"derivedFrom":[makeQuery(id+"F1.opExtrude","CAP_FACE",FACE,{"disambiguationData":[OSD([sQuery(id+"F0.wireOp",EDGE,"E0"),sQuery(id+"F0.wireOp",EDGE,"E7"),sQuery(id+"F0.wireOp",EDGE,"E8"),sQuery(id+"F0.wireOp",EDGE,"E9"),sQuery(id+"F0.wireOp",EDGE,"E10"),sQuery(id+"F0.wireOp",EDGE,"E11.filletArc"),sQuery(id+"F0.wireOp",EDGE,"E12.filletArc"),sQuery(id+"F0.wireOp",EDGE,"E13.MirrorCS"),sQuery(id+"F0.wireOp",EDGE,"E14.MirrorCS"),sQuery(id+"F0.wireOp",EDGE,"E15"),sQuery(id+"F0.wireOp",EDGE,"E16"),sQuery(id+"F0.wireOp",EDGE,"E17"),sQuery(id+"F0.wireOp",EDGE,"E18"),sQuery(id+"F0.wireOp",EDGE,"E19"),sQuery(id+"F0.wireOp",EDGE,"E20"),sQuery(id+"F0.wireOp",EDGE,"E21"),sQuery(id+"F0.wireOp",EDGE,"E22"),sQuery(id+"F0.wireOp",EDGE,"E23.0"),sQuery(id+"F0.wireOp",EDGE,"E23.1"),sQuery(id+"F0.wireOp",EDGE,"E23.2"),sQuery(id+"F0.wireOp",EDGE,"E23.3"),sQuery(id+"F0.wireOp",EDGE,"E23.4"),sQuery(id+"F0.wireOp",EDGE,"E23.5"),sQuery(id+"F0.wireOp",EDGE,"E24.0"),sQuery(id+"F0.wireOp",EDGE,"E24.1"),sQuery(id+"F0.wireOp",EDGE,"E24.2"),sQuery(id+"F0.wireOp",EDGE,"E24.3"),sQuery(id+"F0.wireOp",EDGE,"E24.4"),sQuery(id+"F0.wireOp",EDGE,"E24.5"),sQuery(id+"F0.wireOp",EDGE,"E25.0"),sQuery(id+"F0.wireOp",EDGE,"E25.1"),sQuery(id+"F0.wireOp",EDGE,"E25.2"),sQuery(id+"F0.wireOp",EDGE,"E25.3"),sQuery(id+"F0.wireOp",EDGE,"E25.4"),sQuery(id+"F0.wireOp",EDGE,"E25.5"),sQuery(id+"F0.wireOp",EDGE,"E27.0"),sQuery(id+"F0.wireOp",EDGE,"E27.1"),sQuery(id+"F0.wireOp",EDGE,"E27.2"),sQuery(id+"F0.wireOp",EDGE,"E27.3"),sQuery(id+"F0.wireOp",EDGE,"E27.4"),sQuery(id+"F0.wireOp",EDGE,"E27.5")])],"isStart":true}),makeQuery(id+"F6.opExtrude","SWEPT_FACE",FACE,{"disambiguationData":[OSD([sQuery(id+"F5.wireOp",EDGE,"E33.2.3")])]})]});
            var Q16;
            Q16=makeQuery(id+"F6.boolean.opBoolean","INTERSECT",EDGE,{"derivedFrom":[makeQuery(id+"F1.opExtrude","CAP_FACE",FACE,{"disambiguationData":[OSD([sQuery(id+"F0.wireOp",EDGE,"E0"),sQuery(id+"F0.wireOp",EDGE,"E7"),sQuery(id+"F0.wireOp",EDGE,"E8"),sQuery(id+"F0.wireOp",EDGE,"E9"),sQuery(id+"F0.wireOp",EDGE,"E10"),sQuery(id+"F0.wireOp",EDGE,"E11.filletArc"),sQuery(id+"F0.wireOp",EDGE,"E12.filletArc"),sQuery(id+"F0.wireOp",EDGE,"E13.MirrorCS"),sQuery(id+"F0.wireOp",EDGE,"E14.MirrorCS"),sQuery(id+"F0.wireOp",EDGE,"E15"),sQuery(id+"F0.wireOp",EDGE,"E16"),sQuery(id+"F0.wireOp",EDGE,"E17"),sQuery(id+"F0.wireOp",EDGE,"E18"),sQuery(id+"F0.wireOp",EDGE,"E19"),sQuery(id+"F0.wireOp",EDGE,"E20"),sQuery(id+"F0.wireOp",EDGE,"E21"),sQuery(id+"F0.wireOp",EDGE,"E22"),sQuery(id+"F0.wireOp",EDGE,"E23.0"),sQuery(id+"F0.wireOp",EDGE,"E23.1"),sQuery(id+"F0.wireOp",EDGE,"E23.2"),sQuery(id+"F0.wireOp",EDGE,"E23.3"),sQuery(id+"F0.wireOp",EDGE,"E23.4"),sQuery(id+"F0.wireOp",EDGE,"E23.5"),sQuery(id+"F0.wireOp",EDGE,"E24.0"),sQuery(id+"F0.wireOp",EDGE,"E24.1"),sQuery(id+"F0.wireOp",EDGE,"E24.2"),sQuery(id+"F0.wireOp",EDGE,"E24.3"),sQuery(id+"F0.wireOp",EDGE,"E24.4"),sQuery(id+"F0.wireOp",EDGE,"E24.5"),sQuery(id+"F0.wireOp",EDGE,"E25.0"),sQuery(id+"F0.wireOp",EDGE,"E25.1"),sQuery(id+"F0.wireOp",EDGE,"E25.2"),sQuery(id+"F0.wireOp",EDGE,"E25.3"),sQuery(id+"F0.wireOp",EDGE,"E25.4"),sQuery(id+"F0.wireOp",EDGE,"E25.5"),sQuery(id+"F0.wireOp",EDGE,"E27.0"),sQuery(id+"F0.wireOp",EDGE,"E27.1"),sQuery(id+"F0.wireOp",EDGE,"E27.2"),sQuery(id+"F0.wireOp",EDGE,"E27.3"),sQuery(id+"F0.wireOp",EDGE,"E27.4"),sQuery(id+"F0.wireOp",EDGE,"E27.5")])],"isStart":true}),makeQuery(id+"F6.opExtrude","SWEPT_FACE",FACE,{"disambiguationData":[OSD([sQuery(id+"F5.wireOp",EDGE,"E34.11.3.0")])]})]});
            var Q17;
            Q17=makeQuery(id+"F6.boolean.opBoolean","INTERSECT",EDGE,{"derivedFrom":[makeQuery(id+"F1.opExtrude","CAP_FACE",FACE,{"disambiguationData":[OSD([sQuery(id+"F0.wireOp",EDGE,"E0"),sQuery(id+"F0.wireOp",EDGE,"E7"),sQuery(id+"F0.wireOp",EDGE,"E8"),sQuery(id+"F0.wireOp",EDGE,"E9"),sQuery(id+"F0.wireOp",EDGE,"E10"),sQuery(id+"F0.wireOp",EDGE,"E11.filletArc"),sQuery(id+"F0.wireOp",EDGE,"E12.filletArc"),sQuery(id+"F0.wireOp",EDGE,"E13.MirrorCS"),sQuery(id+"F0.wireOp",EDGE,"E14.MirrorCS"),sQuery(id+"F0.wireOp",EDGE,"E15"),sQuery(id+"F0.wireOp",EDGE,"E16"),sQuery(id+"F0.wireOp",EDGE,"E17"),sQuery(id+"F0.wireOp",EDGE,"E18"),sQuery(id+"F0.wireOp",EDGE,"E19"),sQuery(id+"F0.wireOp",EDGE,"E20"),sQuery(id+"F0.wireOp",EDGE,"E21"),sQuery(id+"F0.wireOp",EDGE,"E22"),sQuery(id+"F0.wireOp",EDGE,"E23.0"),sQuery(id+"F0.wireOp",EDGE,"E23.1"),sQuery(id+"F0.wireOp",EDGE,"E23.2"),sQuery(id+"F0.wireOp",EDGE,"E23.3"),sQuery(id+"F0.wireOp",EDGE,"E23.4"),sQuery(id+"F0.wireOp",EDGE,"E23.5"),sQuery(id+"F0.wireOp",EDGE,"E24.0"),sQuery(id+"F0.wireOp",EDGE,"E24.1"),sQuery(id+"F0.wireOp",EDGE,"E24.2"),sQuery(id+"F0.wireOp",EDGE,"E24.3"),sQuery(id+"F0.wireOp",EDGE,"E24.4"),sQuery(id+"F0.wireOp",EDGE,"E24.5"),sQuery(id+"F0.wireOp",EDGE,"E25.0"),sQuery(id+"F0.wireOp",EDGE,"E25.1"),sQuery(id+"F0.wireOp",EDGE,"E25.2"),sQuery(id+"F0.wireOp",EDGE,"E25.3"),sQuery(id+"F0.wireOp",EDGE,"E25.4"),sQuery(id+"F0.wireOp",EDGE,"E25.5"),sQuery(id+"F0.wireOp",EDGE,"E27.0"),sQuery(id+"F0.wireOp",EDGE,"E27.1"),sQuery(id+"F0.wireOp",EDGE,"E27.2"),sQuery(id+"F0.wireOp",EDGE,"E27.3"),sQuery(id+"F0.wireOp",EDGE,"E27.4"),sQuery(id+"F0.wireOp",EDGE,"E27.5")])],"isStart":true}),makeQuery(id+"F6.opExtrude","SWEPT_FACE",FACE,{"disambiguationData":[OSD([sQuery(id+"F5.wireOp",EDGE,"E34.6.3.0")])]})]});
            var Q18;
            Q18=makeQuery(id+"F6.boolean.opBoolean","INTERSECT",EDGE,{"derivedFrom":[makeQuery(id+"F1.opExtrude","CAP_FACE",FACE,{"disambiguationData":[OSD([sQuery(id+"F0.wireOp",EDGE,"E0"),sQuery(id+"F0.wireOp",EDGE,"E7"),sQuery(id+"F0.wireOp",EDGE,"E8"),sQuery(id+"F0.wireOp",EDGE,"E9"),sQuery(id+"F0.wireOp",EDGE,"E10"),sQuery(id+"F0.wireOp",EDGE,"E11.filletArc"),sQuery(id+"F0.wireOp",EDGE,"E12.filletArc"),sQuery(id+"F0.wireOp",EDGE,"E13.MirrorCS"),sQuery(id+"F0.wireOp",EDGE,"E14.MirrorCS"),sQuery(id+"F0.wireOp",EDGE,"E15"),sQuery(id+"F0.wireOp",EDGE,"E16"),sQuery(id+"F0.wireOp",EDGE,"E17"),sQuery(id+"F0.wireOp",EDGE,"E18"),sQuery(id+"F0.wireOp",EDGE,"E19"),sQuery(id+"F0.wireOp",EDGE,"E20"),sQuery(id+"F0.wireOp",EDGE,"E21"),sQuery(id+"F0.wireOp",EDGE,"E22"),sQuery(id+"F0.wireOp",EDGE,"E23.0"),sQuery(id+"F0.wireOp",EDGE,"E23.1"),sQuery(id+"F0.wireOp",EDGE,"E23.2"),sQuery(id+"F0.wireOp",EDGE,"E23.3"),sQuery(id+"F0.wireOp",EDGE,"E23.4"),sQuery(id+"F0.wireOp",EDGE,"E23.5"),sQuery(id+"F0.wireOp",EDGE,"E24.0"),sQuery(id+"F0.wireOp",EDGE,"E24.1"),sQuery(id+"F0.wireOp",EDGE,"E24.2"),sQuery(id+"F0.wireOp",EDGE,"E24.3"),sQuery(id+"F0.wireOp",EDGE,"E24.4"),sQuery(id+"F0.wireOp",EDGE,"E24.5"),sQuery(id+"F0.wireOp",EDGE,"E25.0"),sQuery(id+"F0.wireOp",EDGE,"E25.1"),sQuery(id+"F0.wireOp",EDGE,"E25.2"),sQuery(id+"F0.wireOp",EDGE,"E25.3"),sQuery(id+"F0.wireOp",EDGE,"E25.4"),sQuery(id+"F0.wireOp",EDGE,"E25.5"),sQuery(id+"F0.wireOp",EDGE,"E27.0"),sQuery(id+"F0.wireOp",EDGE,"E27.1"),sQuery(id+"F0.wireOp",EDGE,"E27.2"),sQuery(id+"F0.wireOp",EDGE,"E27.3"),sQuery(id+"F0.wireOp",EDGE,"E27.4"),sQuery(id+"F0.wireOp",EDGE,"E27.5")])],"isStart":true}),makeQuery(id+"F6.opExtrude","SWEPT_FACE",FACE,{"disambiguationData":[OSD([sQuery(id+"F5.wireOp",EDGE,"E34.7.3.0")])]})]});
            var Q19;
            Q19=makeQuery(id+"F6.boolean.opBoolean","INTERSECT",EDGE,{"derivedFrom":[makeQuery(id+"F1.opExtrude","CAP_FACE",FACE,{"disambiguationData":[OSD([sQuery(id+"F0.wireOp",EDGE,"E0"),sQuery(id+"F0.wireOp",EDGE,"E7"),sQuery(id+"F0.wireOp",EDGE,"E8"),sQuery(id+"F0.wireOp",EDGE,"E9"),sQuery(id+"F0.wireOp",EDGE,"E10"),sQuery(id+"F0.wireOp",EDGE,"E11.filletArc"),sQuery(id+"F0.wireOp",EDGE,"E12.filletArc"),sQuery(id+"F0.wireOp",EDGE,"E13.MirrorCS"),sQuery(id+"F0.wireOp",EDGE,"E14.MirrorCS"),sQuery(id+"F0.wireOp",EDGE,"E15"),sQuery(id+"F0.wireOp",EDGE,"E16"),sQuery(id+"F0.wireOp",EDGE,"E17"),sQuery(id+"F0.wireOp",EDGE,"E18"),sQuery(id+"F0.wireOp",EDGE,"E19"),sQuery(id+"F0.wireOp",EDGE,"E20"),sQuery(id+"F0.wireOp",EDGE,"E21"),sQuery(id+"F0.wireOp",EDGE,"E22"),sQuery(id+"F0.wireOp",EDGE,"E23.0"),sQuery(id+"F0.wireOp",EDGE,"E23.1"),sQuery(id+"F0.wireOp",EDGE,"E23.2"),sQuery(id+"F0.wireOp",EDGE,"E23.3"),sQuery(id+"F0.wireOp",EDGE,"E23.4"),sQuery(id+"F0.wireOp",EDGE,"E23.5"),sQuery(id+"F0.wireOp",EDGE,"E24.0"),sQuery(id+"F0.wireOp",EDGE,"E24.1"),sQuery(id+"F0.wireOp",EDGE,"E24.2"),sQuery(id+"F0.wireOp",EDGE,"E24.3"),sQuery(id+"F0.wireOp",EDGE,"E24.4"),sQuery(id+"F0.wireOp",EDGE,"E24.5"),sQuery(id+"F0.wireOp",EDGE,"E25.0"),sQuery(id+"F0.wireOp",EDGE,"E25.1"),sQuery(id+"F0.wireOp",EDGE,"E25.2"),sQuery(id+"F0.wireOp",EDGE,"E25.3"),sQuery(id+"F0.wireOp",EDGE,"E25.4"),sQuery(id+"F0.wireOp",EDGE,"E25.5"),sQuery(id+"F0.wireOp",EDGE,"E27.0"),sQuery(id+"F0.wireOp",EDGE,"E27.1"),sQuery(id+"F0.wireOp",EDGE,"E27.2"),sQuery(id+"F0.wireOp",EDGE,"E27.3"),sQuery(id+"F0.wireOp",EDGE,"E27.4"),sQuery(id+"F0.wireOp",EDGE,"E27.5")])],"isStart":true}),makeQuery(id+"F6.opExtrude","SWEPT_FACE",FACE,{"disambiguationData":[OSD([sQuery(id+"F5.wireOp",EDGE,"E34.4.3.0")])]})]});
            var Q20;
            Q20=makeQuery(id+"F6.boolean.opBoolean","INTERSECT",EDGE,{"derivedFrom":[makeQuery(id+"F1.opExtrude","CAP_FACE",FACE,{"disambiguationData":[OSD([sQuery(id+"F0.wireOp",EDGE,"E0"),sQuery(id+"F0.wireOp",EDGE,"E7"),sQuery(id+"F0.wireOp",EDGE,"E8"),sQuery(id+"F0.wireOp",EDGE,"E9"),sQuery(id+"F0.wireOp",EDGE,"E10"),sQuery(id+"F0.wireOp",EDGE,"E11.filletArc"),sQuery(id+"F0.wireOp",EDGE,"E12.filletArc"),sQuery(id+"F0.wireOp",EDGE,"E13.MirrorCS"),sQuery(id+"F0.wireOp",EDGE,"E14.MirrorCS"),sQuery(id+"F0.wireOp",EDGE,"E15"),sQuery(id+"F0.wireOp",EDGE,"E16"),sQuery(id+"F0.wireOp",EDGE,"E17"),sQuery(id+"F0.wireOp",EDGE,"E18"),sQuery(id+"F0.wireOp",EDGE,"E19"),sQuery(id+"F0.wireOp",EDGE,"E20"),sQuery(id+"F0.wireOp",EDGE,"E21"),sQuery(id+"F0.wireOp",EDGE,"E22"),sQuery(id+"F0.wireOp",EDGE,"E23.0"),sQuery(id+"F0.wireOp",EDGE,"E23.1"),sQuery(id+"F0.wireOp",EDGE,"E23.2"),sQuery(id+"F0.wireOp",EDGE,"E23.3"),sQuery(id+"F0.wireOp",EDGE,"E23.4"),sQuery(id+"F0.wireOp",EDGE,"E23.5"),sQuery(id+"F0.wireOp",EDGE,"E24.0"),sQuery(id+"F0.wireOp",EDGE,"E24.1"),sQuery(id+"F0.wireOp",EDGE,"E24.2"),sQuery(id+"F0.wireOp",EDGE,"E24.3"),sQuery(id+"F0.wireOp",EDGE,"E24.4"),sQuery(id+"F0.wireOp",EDGE,"E24.5"),sQuery(id+"F0.wireOp",EDGE,"E25.0"),sQuery(id+"F0.wireOp",EDGE,"E25.1"),sQuery(id+"F0.wireOp",EDGE,"E25.2"),sQuery(id+"F0.wireOp",EDGE,"E25.3"),sQuery(id+"F0.wireOp",EDGE,"E25.4"),sQuery(id+"F0.wireOp",EDGE,"E25.5"),sQuery(id+"F0.wireOp",EDGE,"E27.0"),sQuery(id+"F0.wireOp",EDGE,"E27.1"),sQuery(id+"F0.wireOp",EDGE,"E27.2"),sQuery(id+"F0.wireOp",EDGE,"E27.3"),sQuery(id+"F0.wireOp",EDGE,"E27.4"),sQuery(id+"F0.wireOp",EDGE,"E27.5")])],"isStart":true}),makeQuery(id+"F6.opExtrude","SWEPT_FACE",FACE,{"disambiguationData":[OSD([sQuery(id+"F5.wireOp",EDGE,"E33.1.3")])]})]});
            var Q21;
            Q21=makeQuery(id+"F6.boolean.opBoolean","COPY",EDGE,{"derivedFrom":makeQuery(id+"F6.opExtrude","CAP_EDGE",EDGE,{"disambiguationData":[OSD([sQuery(id+"F5.wireOp",EDGE,"E33.1.0")])],"isStart":true})});
            var Q22;
            Q22=makeQuery(id+"F6.boolean.opBoolean","COPY",EDGE,{"derivedFrom":makeQuery(id+"F6.opExtrude","CAP_EDGE",EDGE,{"disambiguationData":[OSD([sQuery(id+"F5.wireOp",EDGE,"E33.1.2")])],"isStart":true})});
            var Q23;
            Q23=makeQuery(id+"F6.boolean.opBoolean","COPY",EDGE,{"derivedFrom":makeQuery(id+"F6.opExtrude","CAP_EDGE",EDGE,{"disambiguationData":[OSD([sQuery(id+"F5.wireOp",EDGE,"E33.2.3")])],"isStart":true})});
            var Q24;
            Q24=makeQuery(id+"F6.boolean.opBoolean","COPY",EDGE,{"derivedFrom":makeQuery(id+"F6.opExtrude","CAP_EDGE",EDGE,{"disambiguationData":[OSD([sQuery(id+"F5.wireOp",EDGE,"E33.2.2")])],"isStart":true})});
            var Q25;
            Q25=makeQuery(id+"F6.boolean.opBoolean","COPY",EDGE,{"derivedFrom":makeQuery(id+"F6.opExtrude","CAP_EDGE",EDGE,{"disambiguationData":[OSD([sQuery(id+"F5.wireOp",EDGE,"E33.2.1")])],"isStart":true})});
            var Q26;
            Q26=makeQuery(id+"F6.boolean.opBoolean","COPY",EDGE,{"derivedFrom":makeQuery(id+"F6.opExtrude","CAP_EDGE",EDGE,{"disambiguationData":[OSD([sQuery(id+"F5.wireOp",EDGE,"E34.11.3.0")])],"isStart":true})});
            var Q27;
            Q27=makeQuery(id+"F6.boolean.opBoolean","COPY",EDGE,{"derivedFrom":makeQuery(id+"F6.opExtrude","CAP_EDGE",EDGE,{"disambiguationData":[OSD([sQuery(id+"F5.wireOp",EDGE,"E34.7.3.0")])],"isStart":true})});
            var Q28;
            Q28=makeQuery(id+"F6.boolean.opBoolean","COPY",EDGE,{"derivedFrom":makeQuery(id+"F6.opExtrude","CAP_EDGE",EDGE,{"disambiguationData":[OSD([sQuery(id+"F5.wireOp",EDGE,"E34.4.3.0")])],"isStart":true})});
            var Q29;
            Q29=makeQuery(id+"F6.boolean.opBoolean","COPY",EDGE,{"derivedFrom":makeQuery(id+"F6.opExtrude","SWEPT_EDGE",EDGE,{"disambiguationData":[OSD([sQuery(id+"F5.wireOp",EDGE,"E33.1.2"),sQuery(id+"F5.wireOp",EDGE,"E33.1.3")])]})});
            var Q30;
            Q30=makeQuery(id+"F6.boolean.opBoolean","COPY",EDGE,{"derivedFrom":makeQuery(id+"F6.opExtrude","SWEPT_EDGE",EDGE,{"disambiguationData":[OSD([sQuery(id+"F5.wireOp",EDGE,"E33.1.0"),sQuery(id+"F5.wireOp",EDGE,"E33.1.3")])]})});
            var Q31;
            Q31=makeQuery(id+"F6.boolean.opBoolean","COPY",EDGE,{"derivedFrom":makeQuery(id+"F6.opExtrude","CAP_EDGE",EDGE,{"disambiguationData":[OSD([sQuery(id+"F5.wireOp",EDGE,"E33.1.1")])],"isStart":true})});
            var Q32;
            Q32=makeQuery(id+"F6.boolean.opBoolean","COPY",EDGE,{"derivedFrom":makeQuery(id+"F6.opExtrude","SWEPT_EDGE",EDGE,{"disambiguationData":[OSD([sQuery(id+"F5.wireOp",EDGE,"E33.1.1"),sQuery(id+"F5.wireOp",EDGE,"E33.1.2")])]})});
            var Q33;
            Q33=makeQuery(id+"F6.boolean.opBoolean","COPY",EDGE,{"derivedFrom":makeQuery(id+"F6.opExtrude","SWEPT_EDGE",EDGE,{"disambiguationData":[OSD([sQuery(id+"F5.wireOp",EDGE,"E33.1.0"),sQuery(id+"F5.wireOp",EDGE,"E33.1.1")])]})});
            var Q34;
            Q34=makeQuery(id+"F6.boolean.opBoolean","COPY",EDGE,{"derivedFrom":makeQuery(id+"F6.opExtrude","SWEPT_EDGE",EDGE,{"disambiguationData":[OSD([sQuery(id+"F5.wireOp",EDGE,"E33.2.0"),sQuery(id+"F5.wireOp",EDGE,"E33.2.3")])]})});
            var Q35;
            Q35=makeQuery(id+"F6.boolean.opBoolean","COPY",EDGE,{"derivedFrom":makeQuery(id+"F6.opExtrude","SWEPT_EDGE",EDGE,{"disambiguationData":[OSD([sQuery(id+"F5.wireOp",EDGE,"E33.2.2"),sQuery(id+"F5.wireOp",EDGE,"E33.2.3")])]})});
            var Q36;
            Q36=makeQuery(id+"F6.boolean.opBoolean","COPY",EDGE,{"derivedFrom":makeQuery(id+"F6.opExtrude","SWEPT_EDGE",EDGE,{"disambiguationData":[OSD([sQuery(id+"F5.wireOp",EDGE,"E33.2.1"),sQuery(id+"F5.wireOp",EDGE,"E33.2.2")])]})});
            var Q37;
            Q37=makeQuery(id+"F6.boolean.opBoolean","COPY",EDGE,{"derivedFrom":makeQuery(id+"F6.opExtrude","SWEPT_EDGE",EDGE,{"disambiguationData":[OSD([sQuery(id+"F5.wireOp",EDGE,"E33.2.0"),sQuery(id+"F5.wireOp",EDGE,"E33.2.1")])]})});
            var Q38;
            Q38=makeQuery(id+"F6.boolean.opBoolean","COPY",EDGE,{"derivedFrom":makeQuery(id+"F6.opExtrude","SWEPT_EDGE",EDGE,{"disambiguationData":[OSD([sQuery(id+"F5.wireOp",EDGE,"E34.6.3.0"),sQuery(id+"F5.wireOp",EDGE,"E34.11.3.0")])]})});
            var Q39;
            Q39=makeQuery(id+"F6.boolean.opBoolean","COPY",EDGE,{"derivedFrom":makeQuery(id+"F6.opExtrude","SWEPT_EDGE",EDGE,{"disambiguationData":[OSD([sQuery(id+"F5.wireOp",EDGE,"E34.7.3.0"),sQuery(id+"F5.wireOp",EDGE,"E34.11.3.0")])]})});
            var Q40;
            Q40=makeQuery(id+"F6.boolean.opBoolean","COPY",EDGE,{"derivedFrom":makeQuery(id+"F6.opExtrude","SWEPT_EDGE",EDGE,{"disambiguationData":[OSD([sQuery(id+"F5.wireOp",EDGE,"E34.4.3.0"),sQuery(id+"F5.wireOp",EDGE,"E34.7.3.0")])]})});
            var Q41;
            Q41=makeQuery(id+"F6.boolean.opBoolean","COPY",EDGE,{"derivedFrom":makeQuery(id+"F6.opExtrude","SWEPT_EDGE",EDGE,{"disambiguationData":[OSD([sQuery(id+"F5.wireOp",EDGE,"E34.4.3.0"),sQuery(id+"F5.wireOp",EDGE,"E34.6.3.0")])]})});
            fillet(context, id + "F7", {"entities" : qUnion([Q0, Q1, Q2, Q3, Q4, Q5, Q6, Q7, Q8, Q9, Q10, Q11, Q12, Q13, Q14, Q15, Q16, Q17, Q18, Q19, Q20, Q21, Q22, Q23, Q24, Q25, Q26, Q27, Q28, Q29, Q30, Q31, Q32, Q33, Q34, Q35, Q36, Q37, Q38, Q39, Q40, Q41]), "radius" : 0.5 * mm, "tangentPropagation" : true, "allowEdgeOverflow" : false});
        }
    });
